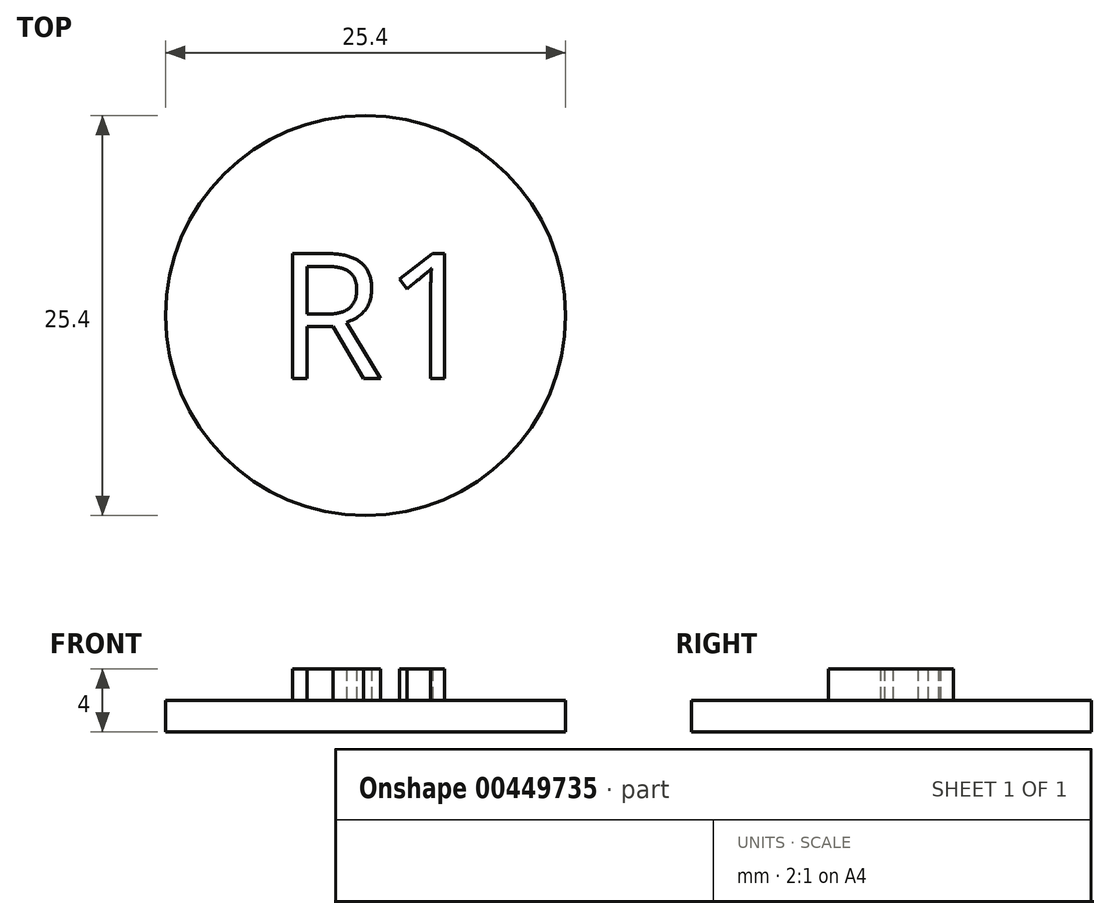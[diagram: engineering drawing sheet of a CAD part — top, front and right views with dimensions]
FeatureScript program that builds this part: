
annotation { "Feature Type Name" : "Feature", "Feature Type Description" : "" }
export const myFeature = defineFeature(function(context is Context, id is Id, definition is map)
    precondition{}
    {
        {
            var Q0;
            Q0=qCreatedBy(makeId("Top.planeOp"),FACE);
            var sketch = newSketch(context, id + "F0", { "sketchPlane" : qUnion([Q0])});
            skCircle(sketch, "E0", {"center": v(0, 0) * mm, "radius": 12.7 * mm});
            skSolve(sketch);
        }
        {
            var Q0;
            Q0 = qSketchRegion(id + "F0", true);
            extrude(context, id + "F1", {"entities" : qUnion([Q0]), "depth" : 2 * mm});
        }
        {
            var Q0;
            Q0=makeQuery(id+"F1.opExtrude","CAP_FACE",FACE,{"disambiguationData":[OSD([sQuery(id+"F0.wireOp",EDGE,"E0")])],"isStart":false});
            var sketch = newSketch(context, id + "F2", { "sketchPlane" : qUnion([Q0])});
            skText(sketch, "E1", { "text": "R1", "fontName": "OpenSans-Regular.ttf"});
            const initialGuessF2  = {"E1": [-0.00573, -0.004, 1, 0, 0.008]};
            skSetInitialGuess(sketch, initialGuessF2);
            skSolve(sketch);
        }
        {
            var Q0;
            Q0 = qSketchRegion(id + "F2", true);
            extrude(context, id + "F3", {"entities" : qUnion([Q0]), "operationType" : NewBodyOperationType.ADD, "depth" : 2 * mm});
        }
    });
